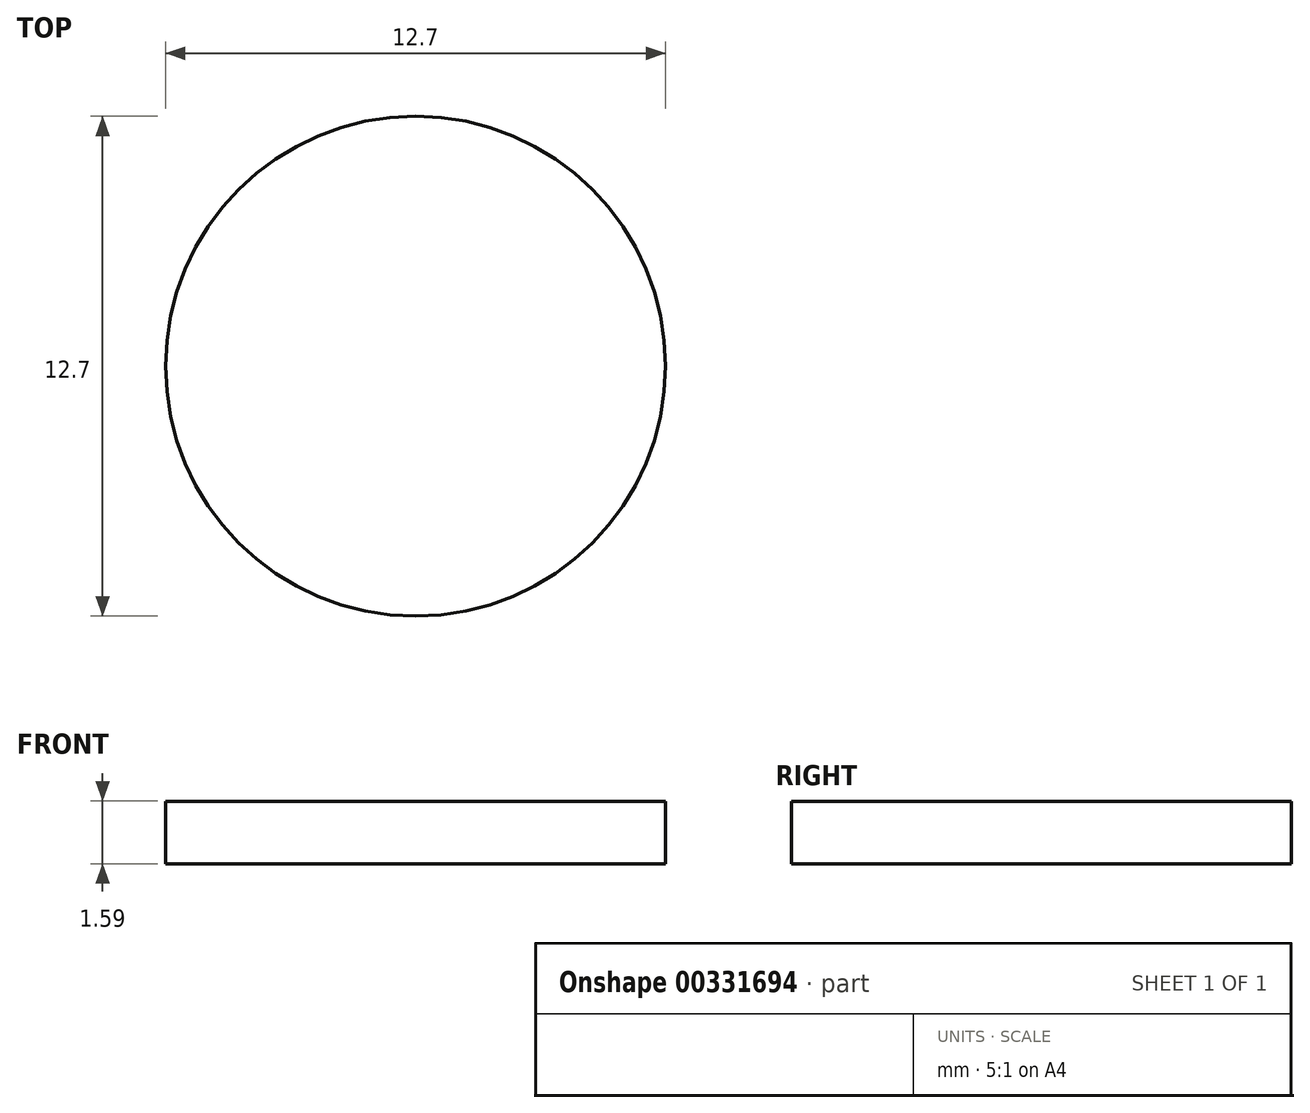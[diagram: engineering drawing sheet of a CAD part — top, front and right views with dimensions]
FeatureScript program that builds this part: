
annotation { "Feature Type Name" : "Feature", "Feature Type Description" : "" }
export const myFeature = defineFeature(function(context is Context, id is Id, definition is map)
    precondition{}
    {
        {
            var Q0;
            Q0=qCreatedBy(makeId("Top.planeOp"),FACE);
            var sketch = newSketch(context, id + "F0", { "sketchPlane" : qUnion([Q0])});
            skCircle(sketch, "E0", {"center": v(0, 0) * mm, "radius": 6.35 * mm});
            skSolve(sketch);
        }
        {
            var Q0;
            Q0 = qSketchRegion(id + "F0", true);
            extrude(context, id + "F1", {"entities" : qUnion([Q0]), "depth" : 1.59 * mm});
        }
    });
